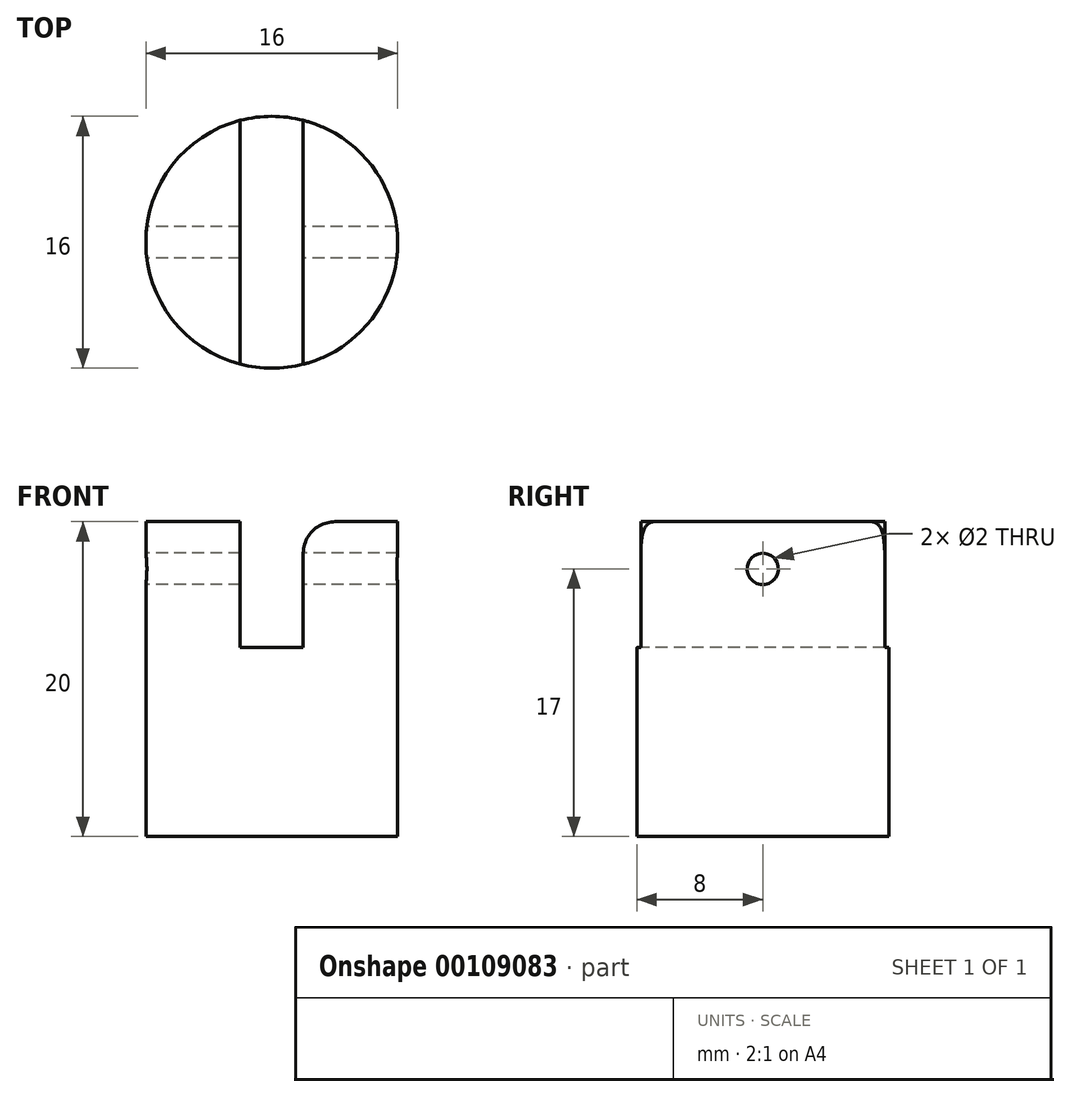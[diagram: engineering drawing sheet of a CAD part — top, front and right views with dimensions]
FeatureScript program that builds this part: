
annotation { "Feature Type Name" : "Feature", "Feature Type Description" : "" }
export const myFeature = defineFeature(function(context is Context, id is Id, definition is map)
    precondition{}
    {
        {
            var Q0;
            Q0=qCreatedBy(makeId("Top.planeOp"),FACE);
            var sketch = newSketch(context, id + "F0", { "sketchPlane" : qUnion([Q0])});
            skCircle(sketch, "E0", {"center": v(0, 0) * mm, "radius": 8 * mm});
            skSolve(sketch);
        }
        {
            var Q0;
            Q0=makeQuery(id+"F0.imprint","IMPRINT",FACE,{"disambiguationData":[TD([[makeQuery(id+"F0.imprint","IMPRINT",EDGE,{"derivedFrom":sQuery(id+"F0.wireOp",EDGE,"E0")}),1.0]])]});
            extrude(context, id + "F1", {"entities" : qUnion([Q0]), "depth" : 20 * mm});
        }
        {
            var Q0;
            Q0=makeQuery(id+"F1.opExtrude","CAP_FACE",FACE,{"disambiguationData":[OSD([sQuery(id+"F0.wireOp",EDGE,"E0")])],"isStart":false});
            var sketch = newSketch(context, id + "F2", { "sketchPlane" : qUnion([Q0])});
            skLineSegment(sketch, "E1.bottom", {"start": v(-2, 8) * mm, "end": v(2, 8) * mm});
            skLineSegment(sketch, "E1.top", {"start": v(-2, -8) * mm, "end": v(2, -8) * mm});
            skLineSegment(sketch, "E1.left", {"start": v(-2, 8) * mm, "end": v(-2, -8) * mm});
            skLineSegment(sketch, "E1.right", {"start": v(2, 8) * mm, "end": v(2, -8) * mm});
            skPoint(sketch, "E1.middle", {"position": v(0, 0) * mm});
            skSolve(sketch);
        }
        {
            var Q0;
            {var subQ0=makeQuery(id+"F1.opExtrude","CAP_EDGE",EDGE,{"disambiguationData":[OSD([sQuery(id+"F0.wireOp",EDGE,"E0")])],"isStart":false});var subQ4=sQuery(id+"F2.wireOp",EDGE,"E1.left");var subQ5=makeQuery(id+"F2.imprint","INTERSECT",VERTEX,{"disambiguationData":[OD(0.0)],"derivedFrom":[subQ0,subQ4]});Q0=makeQuery(id+"F2.imprint","IMPRINT",FACE,{"disambiguationData":[TD([[makeQuery(id+"F2.imprint","IMPRINT",EDGE,{"disambiguationData":[TD([[subQ5,-1.0]])],"derivedFrom":subQ4}),1.0]])]});}
            extrude(context, id + "F3", {"entities" : qUnion([Q0]), "operationType" : NewBodyOperationType.REMOVE, "oppositeDirection" : true, "depth" : 8 * mm});
        }
        {
            var Q0;
            Q0=qCreatedBy(makeId("Right.planeOp"),FACE);
            var sketch = newSketch(context, id + "F4", { "sketchPlane" : qUnion([Q0])});
            skCircle(sketch, "E2", {"center": v(0, 17) * mm, "radius": 1 * mm});
            skSolve(sketch);
        }
        {
            var Q0;
            Q0=makeQuery(id+"F4.imprint","IMPRINT",FACE,{"disambiguationData":[TD([[makeQuery(id+"F4.imprint","IMPRINT",EDGE,{"derivedFrom":sQuery(id+"F4.wireOp",EDGE,"E2")}),1.0]])]});
            extrude(context, id + "F5", {"entities" : qUnion([Q0]), "operationType" : NewBodyOperationType.REMOVE, "endBound" : BoundingType.SYMMETRIC, "depth" : 25 * mm});
        }
        {
            var Q0;
            Q0=makeQuery(id+"F3.boolean.opBoolean","COPY",EDGE,{"derivedFrom":makeQuery(id+"F3.opExtrude","CAP_EDGE",EDGE,{"disambiguationData":[OSD([sQuery(id+"F2.wireOp",EDGE,"E1.left")])],"isStart":true})});
            var Q1;
            Q1=makeQuery(id+"F3.boolean.opBoolean","COPY",EDGE,{"derivedFrom":makeQuery(id+"F3.opExtrude","CAP_EDGE",EDGE,{"disambiguationData":[OSD([sQuery(id+"F2.wireOp",EDGE,"E1.right")])],"isStart":true})});
            fillet(context, id + "F6", {"entities" : qUnion([Q0, Q1]), "radius" : 2 * mm, "tangentPropagation" : true, "allowEdgeOverflow" : false});
        }
    });
